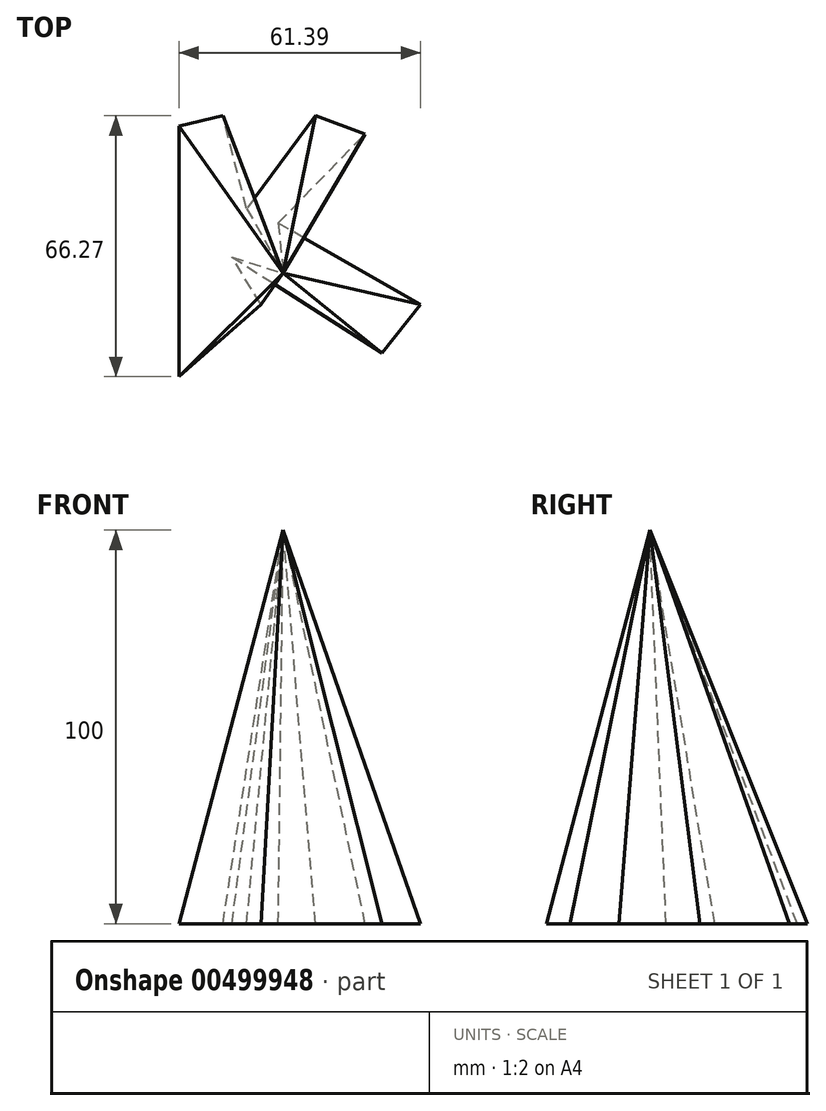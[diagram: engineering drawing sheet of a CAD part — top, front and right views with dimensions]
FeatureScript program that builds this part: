
annotation { "Feature Type Name" : "Feature", "Feature Type Description" : "" }
export const myFeature = defineFeature(function(context is Context, id is Id, definition is map)
    precondition{}
    {
        {
            var Q0;
            Q0=qCreatedBy(makeId("Top.planeOp"),FACE);
            var sketch = newSketch(context, id + "F0", { "sketchPlane" : qUnion([Q0])});
            skLineSegment(sketch, "E0", {"start": v(-34.71, 37.44) * mm, "end": v(-34.71, -26.25) * mm});
            skLineSegment(sketch, "E1", {"start": v(-34.71, -26.25) * mm, "end": v(-13.88, -7.89) * mm});
            skLineSegment(sketch, "E2", {"start": v(-13.88, -7.89) * mm, "end": v(-21.23, 4.16) * mm});
            skLineSegment(sketch, "E3", {"start": v(-21.23, 4.16) * mm, "end": v(16.93, -20.23) * mm});
            skLineSegment(sketch, "E4", {"start": v(16.93, -20.23) * mm, "end": v(26.68, -7.89) * mm});
            skLineSegment(sketch, "E5", {"start": v(26.68, -7.89) * mm, "end": v(-9.47, 12.77) * mm});
            skLineSegment(sketch, "E6", {"start": v(-9.47, 12.77) * mm, "end": v(12.62, 35.43) * mm});
            skLineSegment(sketch, "E7", {"start": v(12.62, 35.43) * mm, "end": v(0, 40.02) * mm});
            skLineSegment(sketch, "E8", {"start": v(0, 40.02) * mm, "end": v(-17.5, 16.5) * mm});
            skLineSegment(sketch, "E9", {"start": v(-17.5, 16.5) * mm, "end": v(-23.52, 40.02) * mm});
            skLineSegment(sketch, "E10", {"start": v(-23.52, 40.02) * mm, "end": v(-34.71, 37.44) * mm});
            skSolve(sketch);
        }
        {
            var Q0;
            Q0=qCreatedBy(makeId("Top.planeOp"),FACE);
            cPlane(context, id + "F1", {"entities" : qUnion([Q0]), "cplaneType" : CPlaneType.OFFSET, "offset" : 100 * mm, "width" : 150 * mm, "height" : 150 * mm});
        }
        {
            var Q0;
            Q0=qCreatedBy(id+"F1.planeOp",FACE);
            var sketch = newSketch(context, id + "F2", { "sketchPlane" : qUnion([Q0])});
            skPoint(sketch, "E11", {"position": v(-8.2, 0) * mm});
            skSolve(sketch);
        }
        {
            var Q0;
            Q0=makeQuery(id+"F0.imprint","IMPRINT",FACE,{"disambiguationData":[TD([[makeQuery(id+"F0.imprint","IMPRINT",EDGE,{"derivedFrom":sQuery(id+"F0.wireOp",EDGE,"E0")}),1.0]])]});
            var Q1;
            Q1=sQuery(id+"F2.wireOp",VERTEX,"E11");
            loft(context, id + "F3", {"sheetProfilesArray" : [{ "sheetProfileEntities" : qUnion([Q0]) }, { "sheetProfileEntities" : qUnion([Q1]) }]});
        }
    });
